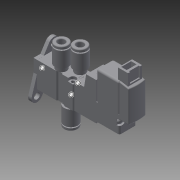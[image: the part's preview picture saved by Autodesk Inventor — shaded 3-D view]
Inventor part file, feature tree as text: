
AUTODESK INVENTOR PART (.ipt)
format: ipt  version: 2014 SP1 (Build 180222100, 222)  size: 743,424 bytes
history: native  units: in
note: dims shown in document units (in); Inventor stores cm internally (conversion verified against a paired STEP export)
features: imported_body x9, other x7, hole x3
ambient origin geometry x8: Origin, YZ Plane, XZ Plane, XY Plane, X Axis, Y Axis, Z Axis, Center Point
bodies: Body1 (feature_tree), Body2 (feature_tree), Body3 (feature_tree), Body4 (feature_tree), Body5 (feature_tree), Body6 (feature_tree), Body7 (feature_tree), Body8 (feature_tree), Body9 (feature_tree)
feature tree (19):
  parser-record x1  (decoder bookkeeping rows leaked as tree rows — omitted from the tree; the rows remain in map.json)
  other  "Pneumatic Solenoid"
  other  "NONE_1"
  other  "NONE_2"
  other  "NONE_3"
  other  "NONE_4"
  other  "NONE_5"
  hole  "Hole"  [1 undecoded]
  hole  "Hole_1"  [1 undecoded]
  hole  "Hole_2"  [1 undecoded]
  imported_body  "Base1"
  imported_body  "Base2"
  imported_body  "Base3"
  imported_body  "Base4"
  imported_body  "Base5"
  imported_body  "Base6"
  imported_body  "Base7"
  imported_body  "Base8"
  imported_body  "Base9"
note: 3 required parameter values undecoded (feature->parameter linkage not recoverable at this tier; creation-order binding heuristic only, values carry confidence <= 0.55)
